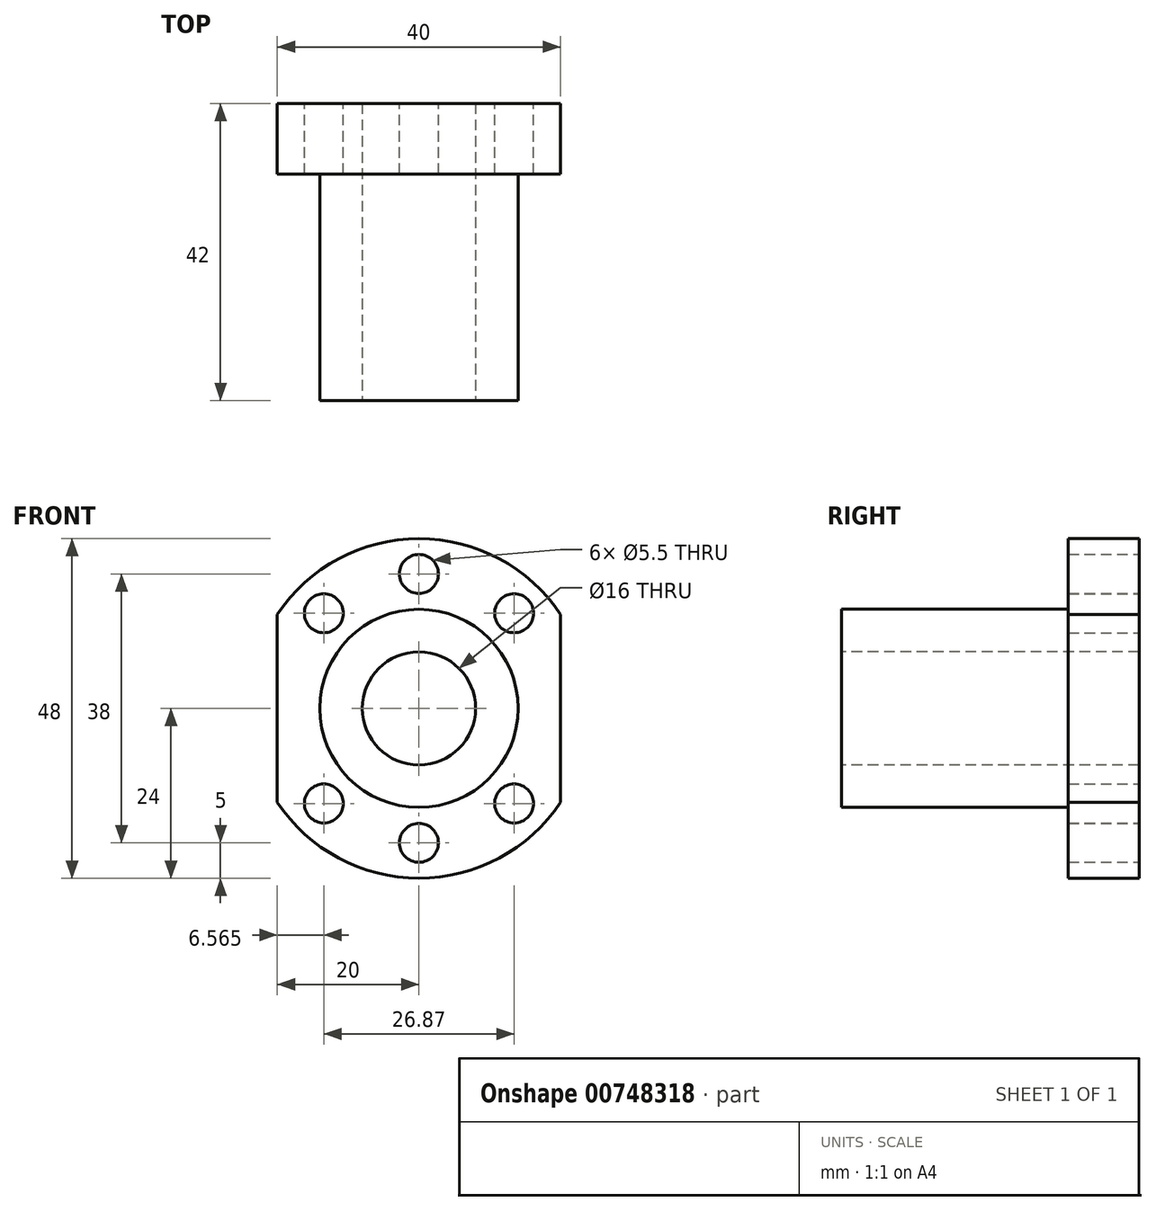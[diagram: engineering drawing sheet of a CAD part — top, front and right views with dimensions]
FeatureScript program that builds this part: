
annotation { "Feature Type Name" : "Feature", "Feature Type Description" : "" }
export const myFeature = defineFeature(function(context is Context, id is Id, definition is map)
    precondition{}
    {
        {
            var Q0;
            Q0=qCreatedBy(makeId("Front.planeOp"),FACE);
            var sketch = newSketch(context, id + "F0", { "sketchPlane" : qUnion([Q0])});
            skArc(sketch, "E0", {"start": v(-20, -13.27) * mm, "mid": v(0, -24) * mm, "end": v(20, -13.27) * mm});
            skLineSegment(sketch, "E1.0", {"start": v(-20, 13.27) * mm, "end": v(-20, -13.27) * mm});
            skLineSegment(sketch, "E2.0", {"start": v(20, 13.27) * mm, "end": v(20, -13.27) * mm});
            skArc(sketch, "E3.trimOffspring", {"start": v(20, 13.27) * mm, "mid": v(0, 24) * mm, "end": v(-20, 13.27) * mm});
            skSolve(sketch);
        }
        {
            var Q0;
            Q0 = qSketchRegion(id + "F0", true);
            extrude(context, id + "F1", {"entities" : qUnion([Q0]), "depth" : 10 * mm, "offsetDistance" : 25.4 * mm});
        }
        {
            var Q0;
            Q0=makeQuery(id+"F1.opExtrude","CAP_FACE",FACE,{"disambiguationData":[OSD([sQuery(id+"F0.wireOp",EDGE,"E0"),sQuery(id+"F0.wireOp",EDGE,"E1.0"),sQuery(id+"F0.wireOp",EDGE,"E2.0"),sQuery(id+"F0.wireOp",EDGE,"E3.trimOffspring")])],"isStart":false});
            var sketch = newSketch(context, id + "F2", { "sketchPlane" : qUnion([Q0])});
            skCircle(sketch, "E4", {"center": v(0, 0) * mm, "radius": 14 * mm});
            skSolve(sketch);
        }
        {
            var Q0;
            Q0 = qSketchRegion(id + "F2", true);
            extrude(context, id + "F3", {"entities" : qUnion([Q0]), "operationType" : NewBodyOperationType.ADD, "depth" : 32 * mm, "offsetDistance" : 25.4 * mm});
        }
        {
            var Q0;
            Q0=makeQuery(id+"F3.opExtrude","CAP_FACE",FACE,{"disambiguationData":[OSD([sQuery(id+"F2.wireOp",EDGE,"E4")])],"isStart":false});
            var sketch = newSketch(context, id + "F4", { "sketchPlane" : qUnion([Q0])});
            skCircle(sketch, "E5", {"center": v(0, 0) * mm, "radius": 8 * mm});
            skSolve(sketch);
        }
        {
            var Q0;
            Q0 = qSketchRegion(id + "F4", true);
            extrude(context, id + "F5", {"entities" : qUnion([Q0]), "operationType" : NewBodyOperationType.REMOVE, "endBound" : BoundingType.THROUGH_ALL, "oppositeDirection" : true, "depth" : 25.4 * mm, "offsetDistance" : 25.4 * mm});
        }
        {
            var Q0;
            Q0=makeQuery(id+"F1.opExtrude","CAP_FACE",FACE,{"disambiguationData":[OSD([sQuery(id+"F0.wireOp",EDGE,"E0"),sQuery(id+"F0.wireOp",EDGE,"E1.0"),sQuery(id+"F0.wireOp",EDGE,"E2.0"),sQuery(id+"F0.wireOp",EDGE,"E3.trimOffspring")])],"isStart":true});
            var sketch = newSketch(context, id + "F6", { "sketchPlane" : qUnion([Q0])});
            skCircle(sketch, "E6", {"center": v(0, 0) * mm, "radius": 19 * mm, "construction": true});
            skCircle(sketch, "E7", {"center": v(0, 19) * mm, "radius": 2.75 * mm});
            skCircle(sketch, "E8.1.0", {"center": v(-13.44, 13.44) * mm, "radius": 2.75 * mm});
            skCircle(sketch, "E8.3.0", {"center": v(-13.44, -13.44) * mm, "radius": 2.75 * mm});
            skCircle(sketch, "E8.4.0", {"center": v(0, -19) * mm, "radius": 2.75 * mm});
            skCircle(sketch, "E8.5.0", {"center": v(13.44, -13.44) * mm, "radius": 2.75 * mm});
            skCircle(sketch, "E8.7.0", {"center": v(13.44, 13.44) * mm, "radius": 2.75 * mm});
            skSolve(sketch);
        }
        {
            var Q0;
            Q0 = qSketchRegion(id + "F6", true);
            extrude(context, id + "F7", {"entities" : qUnion([Q0]), "operationType" : NewBodyOperationType.REMOVE, "endBound" : BoundingType.THROUGH_ALL, "oppositeDirection" : true, "depth" : 25.4 * mm, "offsetDistance" : 25.4 * mm});
        }
    });
